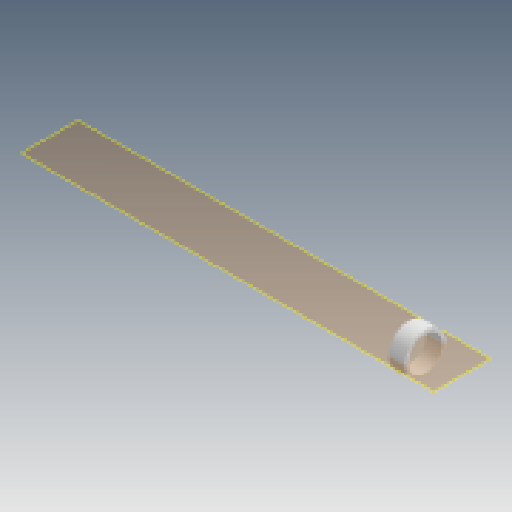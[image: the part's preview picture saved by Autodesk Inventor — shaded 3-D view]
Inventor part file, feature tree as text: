
AUTODESK INVENTOR PART (.ipt)
format: ipt  version: 2025 (Build 290162000, 162)  size: 96,256 bytes
history: native  units: mm
features: other x5, reference x3, plane x1, revolve x1, sketch x1
ambient origin geometry x8: Origin, YZ Plane, XZ Plane, XY Plane, X Axis, Y Axis, Z Axis, Center Point
bodies: 实体1 (feature_tree)
feature tree (11):
  plane  "工作平面2"
  revolve  "旋转1"  Angle=90.0deg
  sketch  "草图1"  dims[d0=18.0mm d1=90.0deg]
  reference  "参考1"
  reference  "参考2"
  reference  "参考3"
  other  "齿轮箱.iam"
  other  "高速轴:1"
  other  "轴承:2"
  other  "滚动轴承 GB/T 276-1994 60000 和 160000 型 6206:1"
  other  "轴:1"
